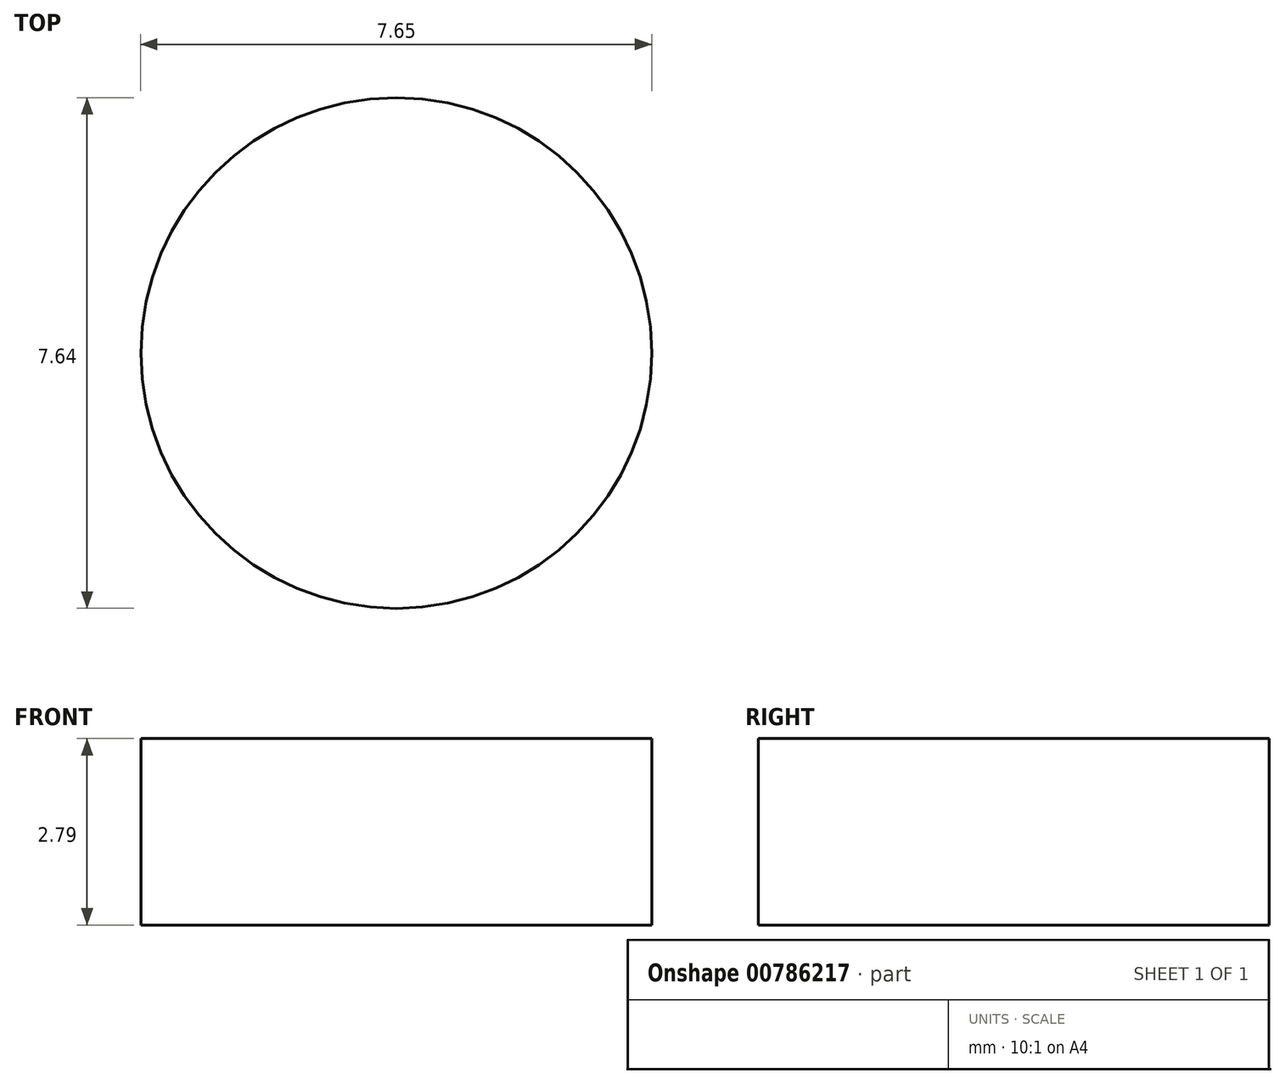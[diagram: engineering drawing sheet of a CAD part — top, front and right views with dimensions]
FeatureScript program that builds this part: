
annotation { "Feature Type Name" : "Feature", "Feature Type Description" : "" }
export const myFeature = defineFeature(function(context is Context, id is Id, definition is map)
    precondition{}
    {
        {
            var Q0;
            Q0=qCreatedBy(makeId("Top.planeOp"),FACE);
            var sketch = newSketch(context, id + "F0", { "sketchPlane" : qUnion([Q0])});
            skCircle(sketch, "E0", {"center": v(-0.4, 0) * mm, "radius": 3.82 * mm});
            skSolve(sketch);
        }
        {
            var Q0;
            Q0=makeQuery(id+"F0.imprint","IMPRINT",FACE,{"disambiguationData":[TD([[makeQuery(id+"F0.imprint","IMPRINT",EDGE,{"derivedFrom":sQuery(id+"F0.wireOp",EDGE,"E0")}),1.0]])]});
            extrude(context, id + "F1", {"entities" : qUnion([Q0]), "depth" : 2.8 * mm, "offsetDistance" : 25.4 * mm});
        }
    });
